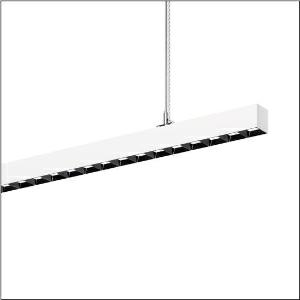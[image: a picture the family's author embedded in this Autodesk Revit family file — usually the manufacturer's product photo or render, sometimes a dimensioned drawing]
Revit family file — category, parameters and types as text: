
# Revit family: silica_r__21_51mx31dc4dwb_7dad
name_source: partatom
category: Lighting Fixtures
units: mm (PartAtom-declared; Revit-internal decimal feet)

## family parameters
Cut with Voids When Loaded = No
Host = Face
Light Source = No
Part Type = Normal
Room Calculation Point = No
Round Connector Dimension = Use Diameter
Shared = No

## types (1)
- --- (1 x LED, 18230 lm, 105.9 W, 4000K)
    Apparent Load = 106 VA
    CIE Flux Codes = 87 99 100 59 100
    Color Rendering = 80
    Color Temperature = 4000K
    Default Elevation = 1800 mm
    Description = Silica® 21, office luminaire, primary light control with darklight reflector, of PMMA, black, CAT 2 (L<= 3000cd/m²), light emission: direct/indirect distribution, primary light characteristic: symmetric, installation type: suspended mounting, LED, rated luminous flux: 18.230lm, luminous efficacy: 172lm/W, light colour: 840, colour temperature: 4000K, with terminal, 3+2-pole, max. 2.5mm², mains connection: 220..240V, AC, 50/60Hz, rated input power: 105.9W, luminaire housing, of aluminium, traffic white (RAL 9016), length: 3.004mm, width: 53mm, height: 53mm, protection rating (complete): IP20, insulation class (complete): insulation class I (protective earthing), certification: CE, permissible operating ambient temperature: 0..+35°C, standard: EN 50419, packaging unit: 1 piece
    Height = 53 mm
    Lamp = 1 x LED
    Lamp Light Flux = 18230 lm
    Lamp Power = 105.9 W
    Lamp count = 1
    Length = 3004 mm
    Luminous efficacy = 172 lm/W
    Manufacturer = Siteco
    ModVariant = No
    Model = 51MX31DC4DWB
    Mounting Place = Ceiling
    Mounting Type = Pendant
    Number of Poles = 1
    OnlyDefault = Yes
    Power Factor = 1
    Product Name = Silica® 21
    Product group = office luminaire | ceiling pendant
    ProductGroupID = 902
    Protection Class = Protection class I
    Protection Degree = IP 20
    RLX_Detail_Level = 1
    RLX_Emergency_Light_Flux = 0 lm
    RLX_Emergency_Type = 0
    RLX_Emergency_Type_DB = No
    RlxData = <blob elided: 64317 chars, md5=b13d699f>
    Socket = socket
    Standby Power = 0 W
    System Light Flux = 18230 lm
    System Power = 106 W
    Type Comments = factory setting: luminous flux: 100 % | dim-lin: 254 | 367 mA
    Type Image = l_1297801.jpg
    URL = http://relux.com
    VarID = @adj_051923
    Voltage = 0 V
    Weight = 0.00 kg
    Width = 53 mm

## geometry (parser evidence)
native form markers: Blend x4, Sweep x11
no freeform markers — native parametric forms only
